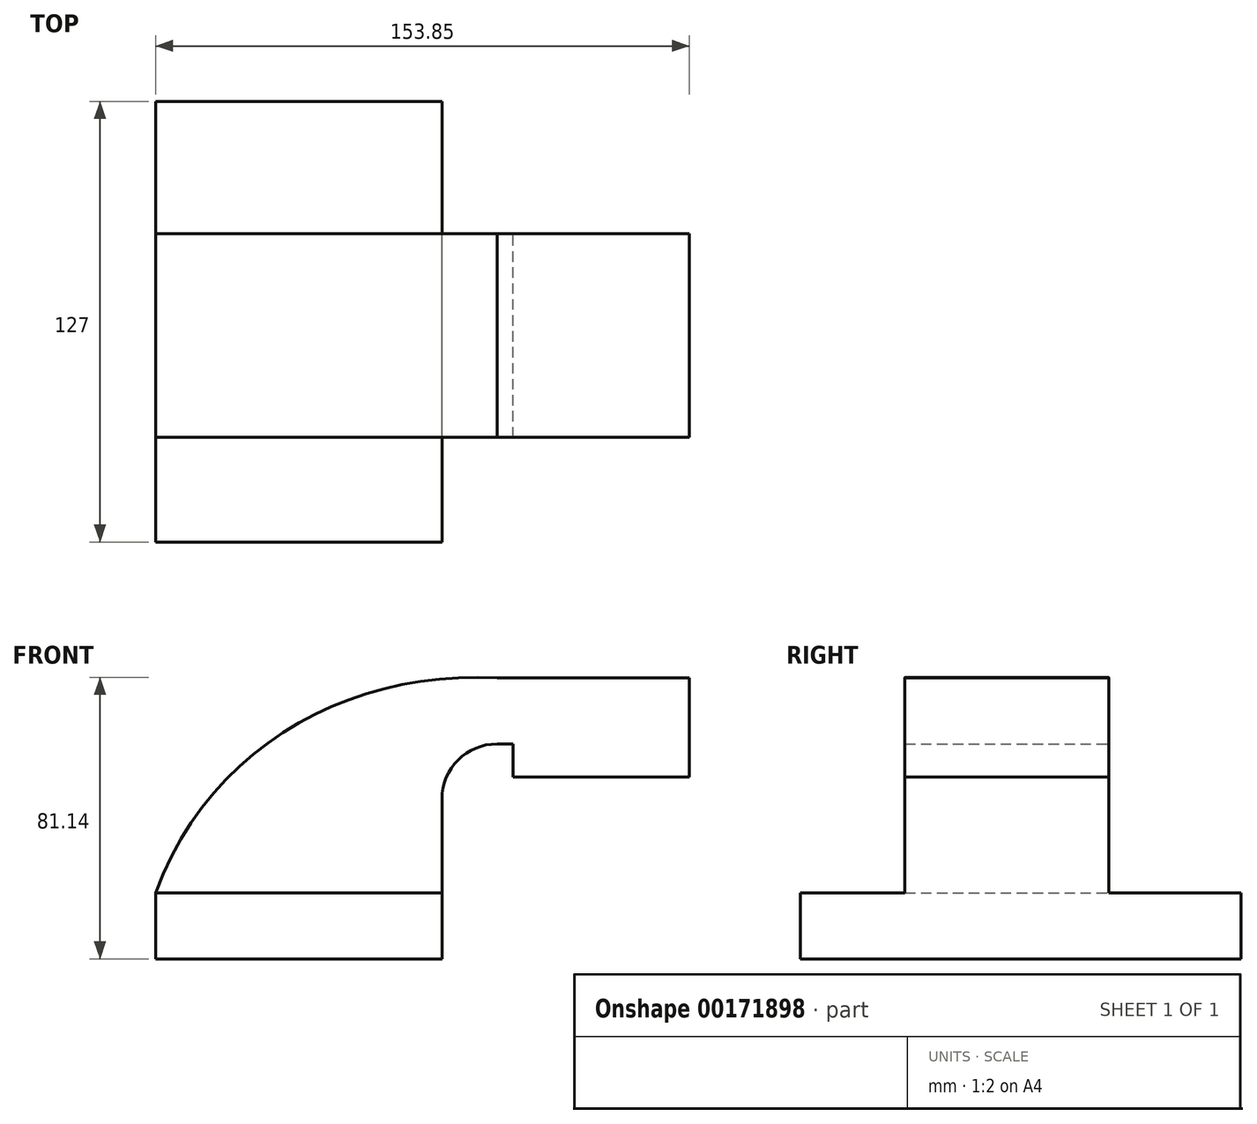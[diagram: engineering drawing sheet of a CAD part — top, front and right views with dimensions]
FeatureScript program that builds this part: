
annotation { "Feature Type Name" : "Feature", "Feature Type Description" : "" }
export const myFeature = defineFeature(function(context is Context, id is Id, definition is map)
    precondition{}
    {
        {
            var Q0;
            Q0=qCreatedBy(makeId("Front.planeOp"),FACE);
            var sketch = newSketch(context, id + "F0", { "sketchPlane" : qUnion([Q0])});
            skLineSegment(sketch, "E0.bottom", {"start": v(-41.28, -9.53) * mm, "end": v(41.28, -9.53) * mm});
            skLineSegment(sketch, "E0.top", {"start": v(-41.28, 9.53) * mm, "end": v(41.28, 9.53) * mm});
            skLineSegment(sketch, "E0.left", {"start": v(-41.28, -9.53) * mm, "end": v(-41.28, 9.53) * mm});
            skLineSegment(sketch, "E0.right", {"start": v(41.28, -9.53) * mm, "end": v(41.28, 9.53) * mm});
            skPoint(sketch, "E0.middle", {"position": v(0, 0) * mm});
            skLineSegment(sketch, "E1.bottom", {"start": v(112.57, 42.88) * mm, "end": v(61.77, 42.88) * mm});
            skLineSegment(sketch, "E1.top", {"start": v(112.57, 71.45) * mm, "end": v(61.77, 71.45) * mm});
            skLineSegment(sketch, "E1.left", {"start": v(112.57, 42.88) * mm, "end": v(112.57, 71.45) * mm});
            skLineSegment(sketch, "E1.right", {"start": v(61.77, 42.88) * mm, "end": v(61.77, 71.45) * mm});
            skPoint(sketch, "E1.middle", {"position": v(87.17, 57.16) * mm});
            skLineSegment(sketch, "E2", {"start": v(41.27, 9.53) * mm, "end": v(41.27, 36.53) * mm});
            skArc(sketch, "E3", {"start": v(41.27, 36.53) * mm, "mid": v(45.92, 47.75) * mm, "end": v(57.15, 52.4) * mm});
            skLineSegment(sketch, "E4", {"start": v(57.15, 52.4) * mm, "end": v(85.72, 52.4) * mm});
            skLineSegment(sketch, "E5.0", {"start": v(57.15, 71.45) * mm, "end": v(85.72, 71.45) * mm});
            skArc(sketch, "E5.1", {"start": v(22.23, 36.53) * mm, "mid": v(32.45, 61.22) * mm, "end": v(57.15, 71.45) * mm});
            skLineSegment(sketch, "E5.2", {"start": v(22.22, 9.53) * mm, "end": v(22.22, 36.53) * mm});
            skLineSegment(sketch, "E6", {"start": v(87.17, 42.88) * mm, "end": v(87.17, 71.45) * mm});
            skFitSpline(sketch, "E7", {"points": [v(-41.28, 9.53) * mm, v(57.15, 71.45) * mm], "startDerivative": vector(46.75, 126.02) * mm, "endDerivative": vector(128.53, -6.81) * mm});
            skSolve(sketch);
        }
        {
            var Q0;
            Q0=makeQuery(id+"F0.imprint","IMPRINT",FACE,{"disambiguationData":[TD([[makeQuery(id+"F0.imprint","IMPRINT",EDGE,{"derivedFrom":sQuery(id+"F0.wireOp",EDGE,"E0.bottom")}),1.0]])]});
            extrude(context, id + "F1", {"entities" : qUnion([Q0]), "endBound" : BoundingType.SYMMETRIC, "depth" : 127 * mm});
        }
        {
            var Q0;
            Q0 = qSketchRegion(id + "F0", true);
            extrude(context, id + "F2", {"entities" : qUnion([Q0]), "operationType" : NewBodyOperationType.ADD, "endBound" : BoundingType.SYMMETRIC, "depth" : 50.8 * mm});
        }
        {
            var Q0;
            Q0 = qSketchRegion(id + "F0", true);
            var Q1;
            Q1=makeQuery(id+"F2.opExtrude","CAP_FACE",FACE,{"disambiguationData":[OSD([sQuery(id+"F0.wireOp",EDGE,"E0.bottom"),sQuery(id+"F0.wireOp",EDGE,"E0.left"),sQuery(id+"F0.wireOp",EDGE,"E0.right"),sQuery(id+"F0.wireOp",EDGE,"E1.bottom"),sQuery(id+"F0.wireOp",EDGE,"E1.top"),sQuery(id+"F0.wireOp",EDGE,"E1.left"),sQuery(id+"F0.wireOp",EDGE,"E1.right"),sQuery(id+"F0.wireOp",EDGE,"E2"),sQuery(id+"F0.wireOp",EDGE,"E3"),sQuery(id+"F0.wireOp",EDGE,"E4"),sQuery(id+"F0.wireOp",EDGE,"E5.0"),sQuery(id+"F0.wireOp",EDGE,"E7")])],"isStart":false});
            extrude(context, id + "F3", {"entities" : qUnion([Q0, Q1]), "operationType" : NewBodyOperationType.ADD, "endBound" : BoundingType.SYMMETRIC, "depth" : 15.88 * mm});
        }
    });
